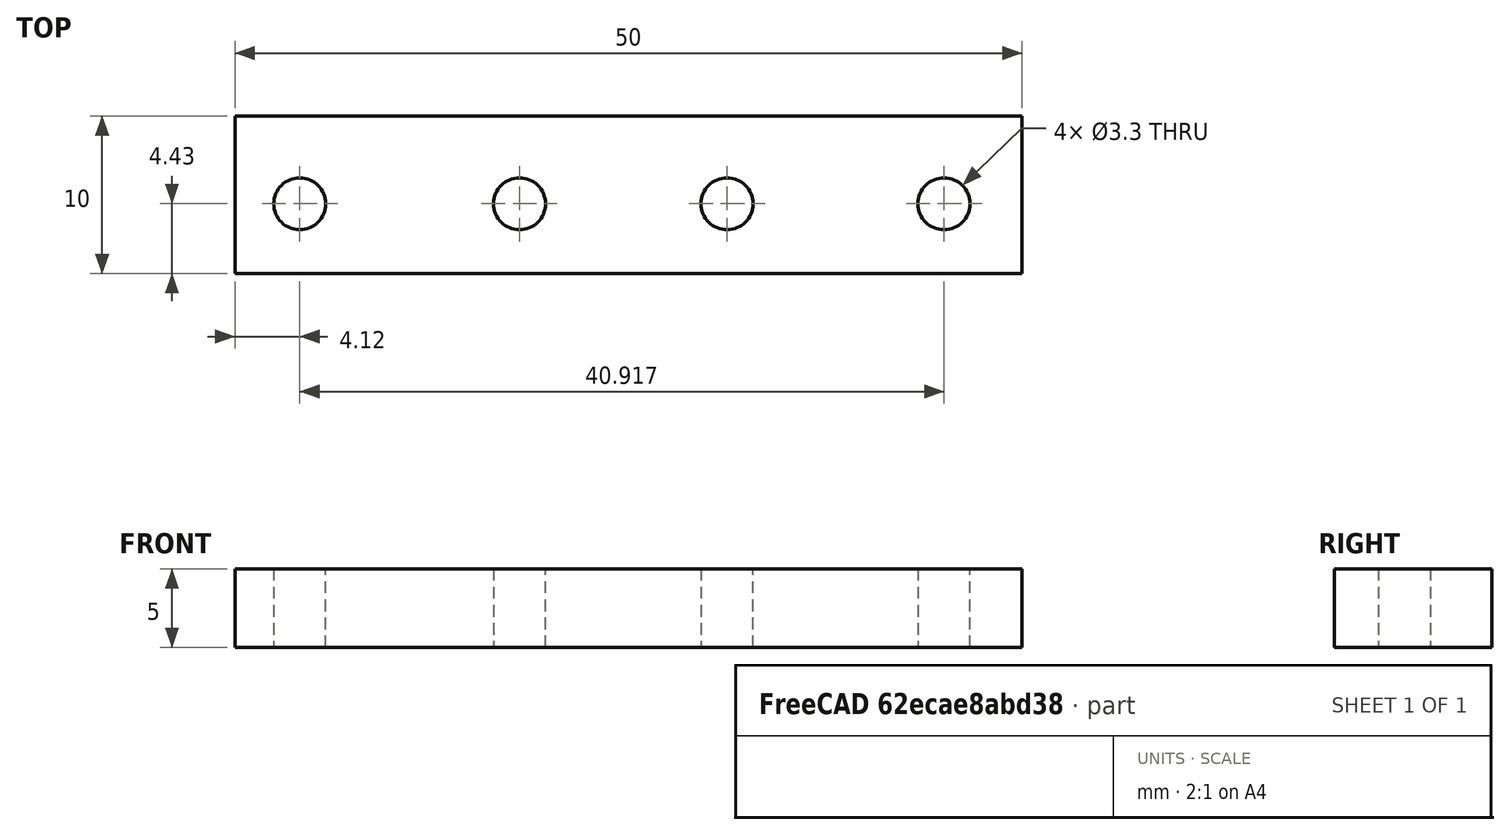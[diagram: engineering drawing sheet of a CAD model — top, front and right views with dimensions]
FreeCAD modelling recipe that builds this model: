
FCSTD DOCUMENT  (FreeCAD 1.0R38806 (Git))
Label: Pieza-mecano
License: All rights reserved
LicenseURL: https://en.wikipedia.org/wiki/All_rights_reserved
objects: Sketcher::SketchObject×1, Part::Extrusion×1
note: 3 computed .brp shape members not serialized (recipe doc carries the construction recipe); baked Part::Feature solids carry a one-line shape summary decoded from their .brp

FEATURE [Sketcher::SketchObject] Sketch
  ArcFitTolerance = 1e-06
  FullyConstrained = false
  MakeInternals = false
  sketch-geometry (8):
    g0: LineSegment StartX=-14.1207 StartY=5.57056 StartZ=0 EndX=-14.1207 EndY=-4.42944 EndZ=0
    g1: LineSegment StartX=-14.1207 StartY=-4.42944 StartZ=0 EndX=35.8793 EndY=-4.42944 EndZ=0
    g2: LineSegment StartX=35.8793 StartY=-4.42944 StartZ=0 EndX=35.8793 EndY=5.57056 EndZ=0
    g3: LineSegment StartX=35.8793 StartY=5.57056 StartZ=0 EndX=-14.1207 EndY=5.57056 EndZ=0
    g4: Circle CenterX=3.95327 CenterY=0 CenterZ=0 NormalX=0 NormalY=0 NormalZ=1 AngleXU=0 Radius=1.65
    g5: Circle CenterX=30.9172 CenterY=0 CenterZ=0 NormalX=0 NormalY=0 NormalZ=1 AngleXU=0 Radius=1.65
    g6: Circle CenterX=-10 CenterY=0 CenterZ=0 NormalX=0 NormalY=0 NormalZ=1 AngleXU=0 Radius=1.65
    g7: Circle CenterX=17.1367 CenterY=0 CenterZ=0 NormalX=0 NormalY=0 NormalZ=1 AngleXU=0 Radius=1.65
  constraints (19):
    c: Coincident(g0,g1)
    c: Coincident(g1,g2)
    c: Coincident(g2,g3)
    c: Coincident(g3,g0)
    c: Vertical(g0)
    c: Vertical(g2)
    c: Horizontal(g1)
    c: Horizontal(g3)
    c: Distance(g2,g2) = 10
    c: Distance(g3,g3) = 50
    c: Diameter(g4) = 3.3
    c: PointOnObject(g4,g-1)
    c: Diameter(g5) = 3.3
    c: PointOnObject(g5,g-1)
    c: Diameter(g6) = 3.3
    c: PointOnObject(g6,g-1)
    c: Diameter(g7) = 3.3
    c: PointOnObject(g7,g-1)
    c: Distance(g6,g-1) = 10
FEATURE [Part::Extrusion] Extrude
  Base = -> Sketch
  Dir = (0,0,1)
  DirMode = 2
  FaceMakerClass = Part::FaceMakerBullseye
  FaceMakerMode = 3
  LengthFwd = 5
  LengthRev = 0
  Solid = true
  Symmetric = false
